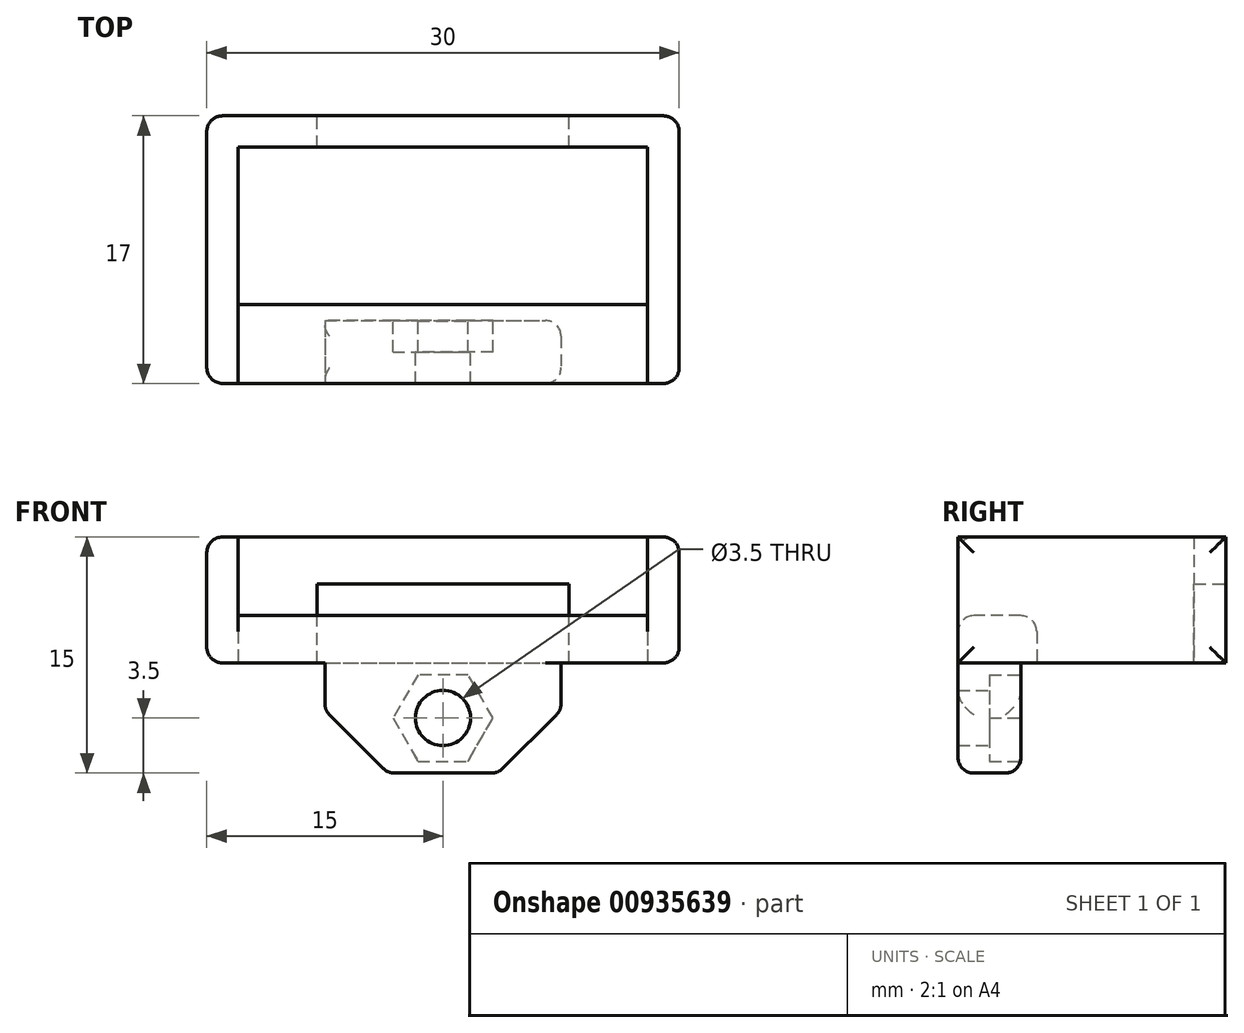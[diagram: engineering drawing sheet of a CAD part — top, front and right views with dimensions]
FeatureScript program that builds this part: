
annotation { "Feature Type Name" : "Feature", "Feature Type Description" : "" }
export const myFeature = defineFeature(function(context is Context, id is Id, definition is map)
    precondition{}
    {
        {
            var Q0;
            Q0=qCreatedBy(makeId("Top.planeOp"),FACE);
            var sketch = newSketch(context, id + "F0", { "sketchPlane" : qUnion([Q0])});
            skLineSegment(sketch, "E0.bottom", {"start": v(13, 7.5) * mm, "end": v(-13, 7.5) * mm});
            skLineSegment(sketch, "E0.top", {"start": v(13, -7.5) * mm, "end": v(-13, -7.5) * mm});
            skLineSegment(sketch, "E0.left", {"start": v(13, 7.5) * mm, "end": v(13, -7.5) * mm});
            skLineSegment(sketch, "E0.right", {"start": v(-13, 7.5) * mm, "end": v(-13, -7.5) * mm});
            skPoint(sketch, "E0.middle", {"position": v(0, 0) * mm});
            skLineSegment(sketch, "E1", {"start": v(-13, -2.5) * mm, "end": v(13, -2.5) * mm});
            skLineSegment(sketch, "E2.bottom", {"start": v(-7.5, -3.5) * mm, "end": v(7.5, -3.5) * mm});
            skLineSegment(sketch, "E2.top", {"start": v(-7.5, -7.5) * mm, "end": v(7.5, -7.5) * mm});
            skLineSegment(sketch, "E2.left", {"start": v(-7.5, -3.5) * mm, "end": v(-7.5, -7.5) * mm});
            skLineSegment(sketch, "E2.right", {"start": v(7.5, -3.5) * mm, "end": v(7.5, -7.5) * mm});
            skPoint(sketch, "E2.middle", {"position": v(0, -5.5) * mm});
            skLineSegment(sketch, "E3.bottom", {"start": v(-15, -7.5) * mm, "end": v(15, -7.5) * mm});
            skLineSegment(sketch, "E3.top", {"start": v(-15, 9.5) * mm, "end": v(15, 9.5) * mm});
            skLineSegment(sketch, "E3.left", {"start": v(-15, -7.5) * mm, "end": v(-15, 9.5) * mm});
            skLineSegment(sketch, "E3.right", {"start": v(15, -7.5) * mm, "end": v(15, 9.5) * mm});
            skPoint(sketch, "E3.middle", {"position": v(0, 1) * mm});
            skSolve(sketch);
        }
        {
            var Q0;
            {var subQ1=sQuery(id+"F0.wireOp",EDGE,"E0.bottom");Q0=makeQuery(id+"F0.imprint","IMPRINT",FACE,{"disambiguationData":[TD([[makeQuery(id+"F0.imprint","IMPRINT",EDGE,{"derivedFrom":subQ1}),-1.0]])]});}
            extrude(context, id + "F1", {"entities" : qUnion([Q0]), "depth" : 8 * mm, "offsetDistance" : 25 * mm});
        }
        {
            var Q0;
            Q0=makeQuery(id+"F0.imprint","IMPRINT",FACE,{"disambiguationData":[TD([[makeQuery(id+"F0.imprint","IMPRINT",EDGE,{"derivedFrom":sQuery(id+"F0.wireOp",EDGE,"E2.bottom")}),-1.0]])]});
            var Q1;
            {var subQ4=sQuery(id+"F0.wireOp",EDGE,"E1");Q1=makeQuery(id+"F0.imprint","IMPRINT",FACE,{"disambiguationData":[TD([[makeQuery(id+"F0.imprint","IMPRINT",EDGE,{"derivedFrom":subQ4}),-1.0]])]});}
            extrude(context, id + "F2", {"entities" : qUnion([Q0, Q1]), "operationType" : NewBodyOperationType.ADD, "depth" : 3 * mm, "offsetDistance" : 25 * mm});
        }
        {
            var Q0;
            Q0=makeQuery(id+"F1.opExtrude","SWEPT_FACE",FACE,{"disambiguationData":[OSD([sQuery(id+"F0.wireOp",EDGE,"E3.top")])]});
            var sketch = newSketch(context, id + "F3", { "sketchPlane" : qUnion([Q0])});
            skLineSegment(sketch, "E4.bottom", {"start": v(-8, 0) * mm, "end": v(8, 0) * mm});
            skLineSegment(sketch, "E4.top", {"start": v(-8, 5) * mm, "end": v(8, 5) * mm});
            skLineSegment(sketch, "E4.left", {"start": v(-8, 0) * mm, "end": v(-8, 5) * mm});
            skLineSegment(sketch, "E4.right", {"start": v(8, 0) * mm, "end": v(8, 5) * mm});
            skPoint(sketch, "E4.middle", {"position": v(0, 2.5) * mm});
            skSolve(sketch);
        }
        {
            var Q0;
            Q0=makeQuery(id+"F3.imprint","IMPRINT",FACE,{"disambiguationData":[TD([[makeQuery(id+"F3.imprint","IMPRINT",EDGE,{"derivedFrom":sQuery(id+"F3.wireOp",EDGE,"E4.bottom")}),-1.0]])]});
            extrude(context, id + "F4", {"entities" : qUnion([Q0]), "operationType" : NewBodyOperationType.REMOVE, "endBound" : BoundingType.UP_TO_NEXT, "oppositeDirection" : true, "depth" : 25 * mm, "offsetDistance" : 25 * mm});
        }
        {
            var Q0;
            Q0=makeQuery(id+"F0.imprint","IMPRINT",FACE,{"disambiguationData":[TD([[makeQuery(id+"F0.imprint","IMPRINT",EDGE,{"derivedFrom":sQuery(id+"F0.wireOp",EDGE,"E2.bottom")}),-1.0]])]});
            extrude(context, id + "F5", {"entities" : qUnion([Q0]), "operationType" : NewBodyOperationType.ADD, "oppositeDirection" : true, "depth" : 7 * mm, "offsetDistance" : 25 * mm});
        }
        {
            var Q0;
            Q0=makeQuery(id+"F5.opExtrude","CAP_EDGE",EDGE,{"disambiguationData":[OSD([sQuery(id+"F0.wireOp",EDGE,"E2.left")])],"isStart":false});
            var Q1;
            Q1=makeQuery(id+"F5.opExtrude","CAP_EDGE",EDGE,{"disambiguationData":[OSD([sQuery(id+"F0.wireOp",EDGE,"E2.right")])],"isStart":false});
            chamfer(context, id + "F6", {"entities" : qUnion([Q0, Q1]), "width" : 4 * mm, "tangentPropagation" : true});
        }
        {
            var Q0;
            Q0=makeQuery(id+"F5.opExtrude","SWEPT_FACE",FACE,{"disambiguationData":[OSD([sQuery(id+"F0.wireOp",EDGE,"E2.bottom")])]});
            var sketch = newSketch(context, id + "F7", { "sketchPlane" : qUnion([Q0])});
            skCircle(sketch, "E5.cCircle", {"center": v(0, -3.5) * mm, "radius": 2.75 * mm, "construction": true});
            skPoint(sketch, "E5.cCircle.perimeterSnap0", {"position": v(0, -7) * mm});
            skLineSegment(sketch, "E5.0", {"start": v(1.59, -6.25) * mm, "end": v(-1.59, -6.25) * mm});
            skLineSegment(sketch, "E5.1", {"start": v(-1.59, -6.25) * mm, "end": v(-3.18, -3.5) * mm});
            skLineSegment(sketch, "E5.2", {"start": v(-3.18, -3.5) * mm, "end": v(-1.59, -0.75) * mm});
            skLineSegment(sketch, "E5.3", {"start": v(-1.59, -0.75) * mm, "end": v(1.59, -0.75) * mm});
            skLineSegment(sketch, "E5.4", {"start": v(1.59, -0.75) * mm, "end": v(3.18, -3.5) * mm});
            skLineSegment(sketch, "E5.5", {"start": v(3.18, -3.5) * mm, "end": v(1.59, -6.25) * mm});
            skPoint(sketch, "E5.0.midPoint", {"position": v(0, -6.25) * mm});
            skPoint(sketch, "E5.0.midPoint.positionSnap0", {"position": v(0, -7) * mm});
            skCircle(sketch, "E6", {"center": v(0, -3.5) * mm, "radius": 1.75 * mm});
            skSolve(sketch);
        }
        {
            var Q0;
            Q0=makeQuery(id+"F7.imprint","IMPRINT",FACE,{"disambiguationData":[TD([[makeQuery(id+"F7.imprint","IMPRINT",EDGE,{"derivedFrom":sQuery(id+"F7.wireOp",EDGE,"E6")}),1.0]])]});
            extrude(context, id + "F8", {"entities" : qUnion([Q0]), "operationType" : NewBodyOperationType.REMOVE, "endBound" : BoundingType.THROUGH_ALL, "oppositeDirection" : true, "depth" : 25 * mm, "offsetDistance" : 25 * mm});
        }
        {
            var Q0;
            Q0=makeQuery(id+"F7.imprint","IMPRINT",FACE,{"disambiguationData":[TD([[makeQuery(id+"F7.imprint","IMPRINT",EDGE,{"derivedFrom":sQuery(id+"F7.wireOp",EDGE,"E5.0")}),-1.0]])]});
            extrude(context, id + "F9", {"entities" : qUnion([Q0]), "operationType" : NewBodyOperationType.REMOVE, "oppositeDirection" : true, "depth" : 2 * mm, "offsetDistance" : 25 * mm});
        }
        {
            var Q0;
            Q0=makeQuery(id+"F5.opExtrude","CAP_EDGE",EDGE,{"disambiguationData":[OSD([sQuery(id+"F0.wireOp",EDGE,"E2.bottom")])],"isStart":false});
            var Q1;
            Q1=makeQuery(id+"F5.opExtrude","CAP_EDGE",EDGE,{"disambiguationData":[OSD([sQuery(id+"F0.wireOp",EDGE,"E0.top")])],"isStart":false});
            var Q2;
            {var subQ0=sQuery(id+"F0.wireOp",EDGE,"E2.left");Q2=makeQuery(id+"F6.opChamfer","BLEND_EDGE",EDGE,{"blendedFrom":[makeQuery(id+"F5.opExtrude","CAP_EDGE",EDGE,{"disambiguationData":[OSD([subQ0])],"isStart":false}),makeQuery(id+"F5.opExtrude","CAP_FACE",FACE,{"disambiguationData":[OSD([sQuery(id+"F0.wireOp",EDGE,"E0.top"),sQuery(id+"F0.wireOp",EDGE,"E2.bottom"),subQ0,sQuery(id+"F0.wireOp",EDGE,"E2.right")])],"isStart":false})],"blendedInto":[makeQuery(id+"F5.opExtrude","CAP_FACE",FACE,{"disambiguationData":[OSD([sQuery(id+"F0.wireOp",EDGE,"E0.top"),sQuery(id+"F0.wireOp",EDGE,"E2.bottom"),subQ0,sQuery(id+"F0.wireOp",EDGE,"E2.right")])],"isStart":false})]});}
            var Q3;
            {var subQ0=sQuery(id+"F0.wireOp",EDGE,"E2.right");Q3=makeQuery(id+"F6.opChamfer","BLEND_EDGE",EDGE,{"blendedFrom":[makeQuery(id+"F5.opExtrude","CAP_EDGE",EDGE,{"disambiguationData":[OSD([subQ0])],"isStart":false}),makeQuery(id+"F5.opExtrude","CAP_FACE",FACE,{"disambiguationData":[OSD([sQuery(id+"F0.wireOp",EDGE,"E0.top"),sQuery(id+"F0.wireOp",EDGE,"E2.bottom"),sQuery(id+"F0.wireOp",EDGE,"E2.left"),subQ0])],"isStart":false})],"blendedInto":[makeQuery(id+"F5.opExtrude","CAP_FACE",FACE,{"disambiguationData":[OSD([sQuery(id+"F0.wireOp",EDGE,"E0.top"),sQuery(id+"F0.wireOp",EDGE,"E2.bottom"),sQuery(id+"F0.wireOp",EDGE,"E2.left"),subQ0])],"isStart":false})]});}
            var Q4;
            Q4=makeQuery(id+"F6.opChamfer","BLEND_EDGE",EDGE,{"blendedFrom":[makeQuery(id+"F5.opExtrude","CAP_EDGE",EDGE,{"disambiguationData":[OSD([sQuery(id+"F0.wireOp",EDGE,"E2.right")])],"isStart":false}),makeQuery(id+"F5.opExtrude","SWEPT_FACE",FACE,{"disambiguationData":[OSD([sQuery(id+"F0.wireOp",EDGE,"E2.bottom")])]})],"blendedInto":[makeQuery(id+"F5.opExtrude","SWEPT_FACE",FACE,{"disambiguationData":[OSD([sQuery(id+"F0.wireOp",EDGE,"E2.bottom")])]})]});
            var Q5;
            {var subQ0=sQuery(id+"F0.wireOp",EDGE,"E0.top");var subQ1=sQuery(id+"F0.wireOp",EDGE,"E3.bottom");Q5=makeQuery(id+"F6.opChamfer","BLEND_EDGE",EDGE,{"blendedFrom":[makeQuery(id+"F5.opExtrude","CAP_EDGE",EDGE,{"disambiguationData":[OSD([sQuery(id+"F0.wireOp",EDGE,"E2.right")])],"isStart":false}),makeQuery(id+"F5.boolean.opBoolean","MERGE",FACE,{"derivedFrom":[makeQuery(id+"F2.boolean.opBoolean","MERGE",FACE,{"derivedFrom":[makeQuery(id+"F1.opExtrude","SWEPT_FACE",FACE,{"disambiguationData":[OSD([subQ1]),TDD([makeQuery(id+"F0.imprint","IMPRINT",EDGE,{"disambiguationData":[TD([[makeQuery(id+"F0.imprint","INTERSECT",VERTEX,{"derivedFrom":[subQ1,sQuery(id+"F0.wireOp",EDGE,"E3.left")]}),-1.0]])],"derivedFrom":subQ1})])]}),makeQuery(id+"F1.opExtrude","SWEPT_FACE",FACE,{"disambiguationData":[OSD([subQ1]),TDD([makeQuery(id+"F0.imprint","IMPRINT",EDGE,{"disambiguationData":[TD([[makeQuery(id+"F0.imprint","INTERSECT",VERTEX,{"derivedFrom":[subQ1,sQuery(id+"F0.wireOp",EDGE,"E3.right")]}),1.0]])],"derivedFrom":subQ1})])]}),makeQuery(id+"F2.opExtrude","SWEPT_FACE",FACE,{"disambiguationData":[OSD([subQ0])]})]}),makeQuery(id+"F5.opExtrude","SWEPT_FACE",FACE,{"disambiguationData":[OSD([subQ0])]})]})],"blendedInto":[makeQuery(id+"F5.boolean.opBoolean","MERGE",FACE,{"derivedFrom":[makeQuery(id+"F2.boolean.opBoolean","MERGE",FACE,{"derivedFrom":[makeQuery(id+"F1.opExtrude","SWEPT_FACE",FACE,{"disambiguationData":[OSD([subQ1]),TDD([makeQuery(id+"F0.imprint","IMPRINT",EDGE,{"disambiguationData":[TD([[makeQuery(id+"F0.imprint","INTERSECT",VERTEX,{"derivedFrom":[subQ1,sQuery(id+"F0.wireOp",EDGE,"E3.left")]}),-1.0]])],"derivedFrom":subQ1})])]}),makeQuery(id+"F1.opExtrude","SWEPT_FACE",FACE,{"disambiguationData":[OSD([subQ1]),TDD([makeQuery(id+"F0.imprint","IMPRINT",EDGE,{"disambiguationData":[TD([[makeQuery(id+"F0.imprint","INTERSECT",VERTEX,{"derivedFrom":[subQ1,sQuery(id+"F0.wireOp",EDGE,"E3.right")]}),1.0]])],"derivedFrom":subQ1})])]}),makeQuery(id+"F2.opExtrude","SWEPT_FACE",FACE,{"disambiguationData":[OSD([subQ0])]})]}),makeQuery(id+"F5.opExtrude","SWEPT_FACE",FACE,{"disambiguationData":[OSD([subQ0])]})]})]});}
            var Q6;
            {var subQ0=sQuery(id+"F0.wireOp",EDGE,"E2.right");Q6=makeQuery(id+"F6.opChamfer","BLEND_EDGE",EDGE,{"blendedFrom":[makeQuery(id+"F5.opExtrude","CAP_EDGE",EDGE,{"disambiguationData":[OSD([subQ0])],"isStart":false}),makeQuery(id+"F5.opExtrude","SWEPT_FACE",FACE,{"disambiguationData":[OSD([subQ0])]})],"blendedInto":[makeQuery(id+"F5.opExtrude","SWEPT_FACE",FACE,{"disambiguationData":[OSD([subQ0])]})]});}
            var Q7;
            Q7=makeQuery(id+"F5.opExtrude","SWEPT_EDGE",EDGE,{"disambiguationData":[OSD([sQuery(id+"F0.wireOp",EDGE,"E0.top"),sQuery(id+"F0.wireOp",EDGE,"E2.right")])]});
            var Q8;
            Q8=makeQuery(id+"F5.opExtrude","CAP_EDGE",EDGE,{"disambiguationData":[OSD([sQuery(id+"F0.wireOp",EDGE,"E2.right")])],"isStart":true});
            var Q9;
            Q9=makeQuery(id+"F5.opExtrude","SWEPT_EDGE",EDGE,{"disambiguationData":[OSD([sQuery(id+"F0.wireOp",EDGE,"E2.bottom"),sQuery(id+"F0.wireOp",EDGE,"E2.right")])]});
            var Q10;
            Q10=makeQuery(id+"F6.opChamfer","BLEND_EDGE",EDGE,{"blendedFrom":[makeQuery(id+"F5.opExtrude","CAP_EDGE",EDGE,{"disambiguationData":[OSD([sQuery(id+"F0.wireOp",EDGE,"E2.left")])],"isStart":false}),makeQuery(id+"F5.opExtrude","SWEPT_FACE",FACE,{"disambiguationData":[OSD([sQuery(id+"F0.wireOp",EDGE,"E2.bottom")])]})],"blendedInto":[makeQuery(id+"F5.opExtrude","SWEPT_FACE",FACE,{"disambiguationData":[OSD([sQuery(id+"F0.wireOp",EDGE,"E2.bottom")])]})]});
            var Q11;
            {var subQ0=sQuery(id+"F0.wireOp",EDGE,"E0.top");var subQ1=sQuery(id+"F0.wireOp",EDGE,"E3.bottom");Q11=makeQuery(id+"F6.opChamfer","BLEND_EDGE",EDGE,{"blendedFrom":[makeQuery(id+"F5.opExtrude","CAP_EDGE",EDGE,{"disambiguationData":[OSD([sQuery(id+"F0.wireOp",EDGE,"E2.left")])],"isStart":false}),makeQuery(id+"F5.boolean.opBoolean","MERGE",FACE,{"derivedFrom":[makeQuery(id+"F2.boolean.opBoolean","MERGE",FACE,{"derivedFrom":[makeQuery(id+"F1.opExtrude","SWEPT_FACE",FACE,{"disambiguationData":[OSD([subQ1]),TDD([makeQuery(id+"F0.imprint","IMPRINT",EDGE,{"disambiguationData":[TD([[makeQuery(id+"F0.imprint","INTERSECT",VERTEX,{"derivedFrom":[subQ1,sQuery(id+"F0.wireOp",EDGE,"E3.left")]}),-1.0]])],"derivedFrom":subQ1})])]}),makeQuery(id+"F1.opExtrude","SWEPT_FACE",FACE,{"disambiguationData":[OSD([subQ1]),TDD([makeQuery(id+"F0.imprint","IMPRINT",EDGE,{"disambiguationData":[TD([[makeQuery(id+"F0.imprint","INTERSECT",VERTEX,{"derivedFrom":[subQ1,sQuery(id+"F0.wireOp",EDGE,"E3.right")]}),1.0]])],"derivedFrom":subQ1})])]}),makeQuery(id+"F2.opExtrude","SWEPT_FACE",FACE,{"disambiguationData":[OSD([subQ0])]})]}),makeQuery(id+"F5.opExtrude","SWEPT_FACE",FACE,{"disambiguationData":[OSD([subQ0])]})]})],"blendedInto":[makeQuery(id+"F5.boolean.opBoolean","MERGE",FACE,{"derivedFrom":[makeQuery(id+"F2.boolean.opBoolean","MERGE",FACE,{"derivedFrom":[makeQuery(id+"F1.opExtrude","SWEPT_FACE",FACE,{"disambiguationData":[OSD([subQ1]),TDD([makeQuery(id+"F0.imprint","IMPRINT",EDGE,{"disambiguationData":[TD([[makeQuery(id+"F0.imprint","INTERSECT",VERTEX,{"derivedFrom":[subQ1,sQuery(id+"F0.wireOp",EDGE,"E3.left")]}),-1.0]])],"derivedFrom":subQ1})])]}),makeQuery(id+"F1.opExtrude","SWEPT_FACE",FACE,{"disambiguationData":[OSD([subQ1]),TDD([makeQuery(id+"F0.imprint","IMPRINT",EDGE,{"disambiguationData":[TD([[makeQuery(id+"F0.imprint","INTERSECT",VERTEX,{"derivedFrom":[subQ1,sQuery(id+"F0.wireOp",EDGE,"E3.right")]}),1.0]])],"derivedFrom":subQ1})])]}),makeQuery(id+"F2.opExtrude","SWEPT_FACE",FACE,{"disambiguationData":[OSD([subQ0])]})]}),makeQuery(id+"F5.opExtrude","SWEPT_FACE",FACE,{"disambiguationData":[OSD([subQ0])]})]})]});}
            var Q12;
            {var subQ0=sQuery(id+"F0.wireOp",EDGE,"E2.left");Q12=makeQuery(id+"F6.opChamfer","BLEND_EDGE",EDGE,{"blendedFrom":[makeQuery(id+"F5.opExtrude","CAP_EDGE",EDGE,{"disambiguationData":[OSD([subQ0])],"isStart":false}),makeQuery(id+"F5.opExtrude","SWEPT_FACE",FACE,{"disambiguationData":[OSD([subQ0])]})],"blendedInto":[makeQuery(id+"F5.opExtrude","SWEPT_FACE",FACE,{"disambiguationData":[OSD([subQ0])]})]});}
            var Q13;
            Q13=makeQuery(id+"F5.opExtrude","CAP_EDGE",EDGE,{"disambiguationData":[OSD([sQuery(id+"F0.wireOp",EDGE,"E2.left")])],"isStart":true});
            var Q14;
            Q14=makeQuery(id+"F1.opExtrude","SWEPT_EDGE",EDGE,{"disambiguationData":[OSD([sQuery(id+"F0.wireOp",EDGE,"E3.top"),sQuery(id+"F0.wireOp",EDGE,"E3.right")])]});
            var Q15;
            Q15=makeQuery(id+"F1.opExtrude","SWEPT_EDGE",EDGE,{"disambiguationData":[OSD([sQuery(id+"F0.wireOp",EDGE,"E3.top"),sQuery(id+"F0.wireOp",EDGE,"E3.left")])]});
            var Q16;
            Q16=makeQuery(id+"F4.boolean.opBoolean","COPY",EDGE,{"derivedFrom":makeQuery(id+"F4.opExtrude","SWEPT_EDGE",EDGE,{"disambiguationData":[OSD([sQuery(id+"F0.wireOp",EDGE,"E3.top"),sQuery(id+"F3.wireOp",EDGE,"E4.bottom"),sQuery(id+"F3.wireOp",EDGE,"E4.right")])]})});
            var Q17;
            Q17=makeQuery(id+"F4.boolean.opBoolean","COPY",EDGE,{"derivedFrom":makeQuery(id+"F4.opExtrude","SWEPT_EDGE",EDGE,{"disambiguationData":[OSD([sQuery(id+"F0.wireOp",EDGE,"E3.top"),sQuery(id+"F3.wireOp",EDGE,"E4.bottom"),sQuery(id+"F3.wireOp",EDGE,"E4.left")])]})});
            var Q18;
            {var subQ0=sQuery(id+"F0.wireOp",EDGE,"E3.bottom");Q18=makeQuery(id+"F1.opExtrude","CAP_EDGE",EDGE,{"disambiguationData":[OSD([subQ0]),TDD([makeQuery(id+"F0.imprint","IMPRINT",EDGE,{"disambiguationData":[TD([[makeQuery(id+"F0.imprint","INTERSECT",VERTEX,{"derivedFrom":[subQ0,sQuery(id+"F0.wireOp",EDGE,"E3.left")]}),-1.0]])],"derivedFrom":subQ0})])],"isStart":false});}
            var Q19;
            Q19=makeQuery(id+"F1.opExtrude","SWEPT_EDGE",EDGE,{"disambiguationData":[OSD([sQuery(id+"F0.wireOp",EDGE,"E3.bottom"),sQuery(id+"F0.wireOp",EDGE,"E3.left")])]});
            var Q20;
            Q20=makeQuery(id+"F1.opExtrude","CAP_EDGE",EDGE,{"disambiguationData":[OSD([sQuery(id+"F0.wireOp",EDGE,"E3.left")])],"isStart":false});
            var Q21;
            Q21=makeQuery(id+"F1.opExtrude","SWEPT_EDGE",EDGE,{"disambiguationData":[OSD([sQuery(id+"F0.wireOp",EDGE,"E3.bottom"),sQuery(id+"F0.wireOp",EDGE,"E3.right")])]});
            var Q22;
            Q22=makeQuery(id+"F1.opExtrude","CAP_EDGE",EDGE,{"disambiguationData":[OSD([sQuery(id+"F0.wireOp",EDGE,"E3.right")])],"isStart":true});
            var Q23;
            Q23=makeQuery(id+"F1.opExtrude","CAP_EDGE",EDGE,{"disambiguationData":[OSD([sQuery(id+"F0.wireOp",EDGE,"E3.right")])],"isStart":false});
            var Q24;
            Q24=makeQuery(id+"F1.opExtrude","CAP_EDGE",EDGE,{"disambiguationData":[OSD([sQuery(id+"F0.wireOp",EDGE,"E3.left")])],"isStart":true});
            var Q25;
            Q25=makeQuery(id+"F2.opExtrude","CAP_EDGE",EDGE,{"disambiguationData":[OSD([sQuery(id+"F0.wireOp",EDGE,"E1")])],"isStart":false});
            var Q26;
            Q26=makeQuery(id+"F2.opExtrude","CAP_EDGE",EDGE,{"disambiguationData":[OSD([sQuery(id+"F0.wireOp",EDGE,"E0.top")])],"isStart":false});
            fillet(context, id + "F10", {"entities" : qUnion([Q0, Q1, Q2, Q3, Q4, Q5, Q6, Q7, Q8, Q9, Q10, Q11, Q12, Q13, Q14, Q15, Q16, Q17, Q18, Q19, Q20, Q21, Q22, Q23, Q24, Q25, Q26]), "radius" : 1 * mm, "tangentPropagation" : true, "allowEdgeOverflow" : false});
        }
    });
